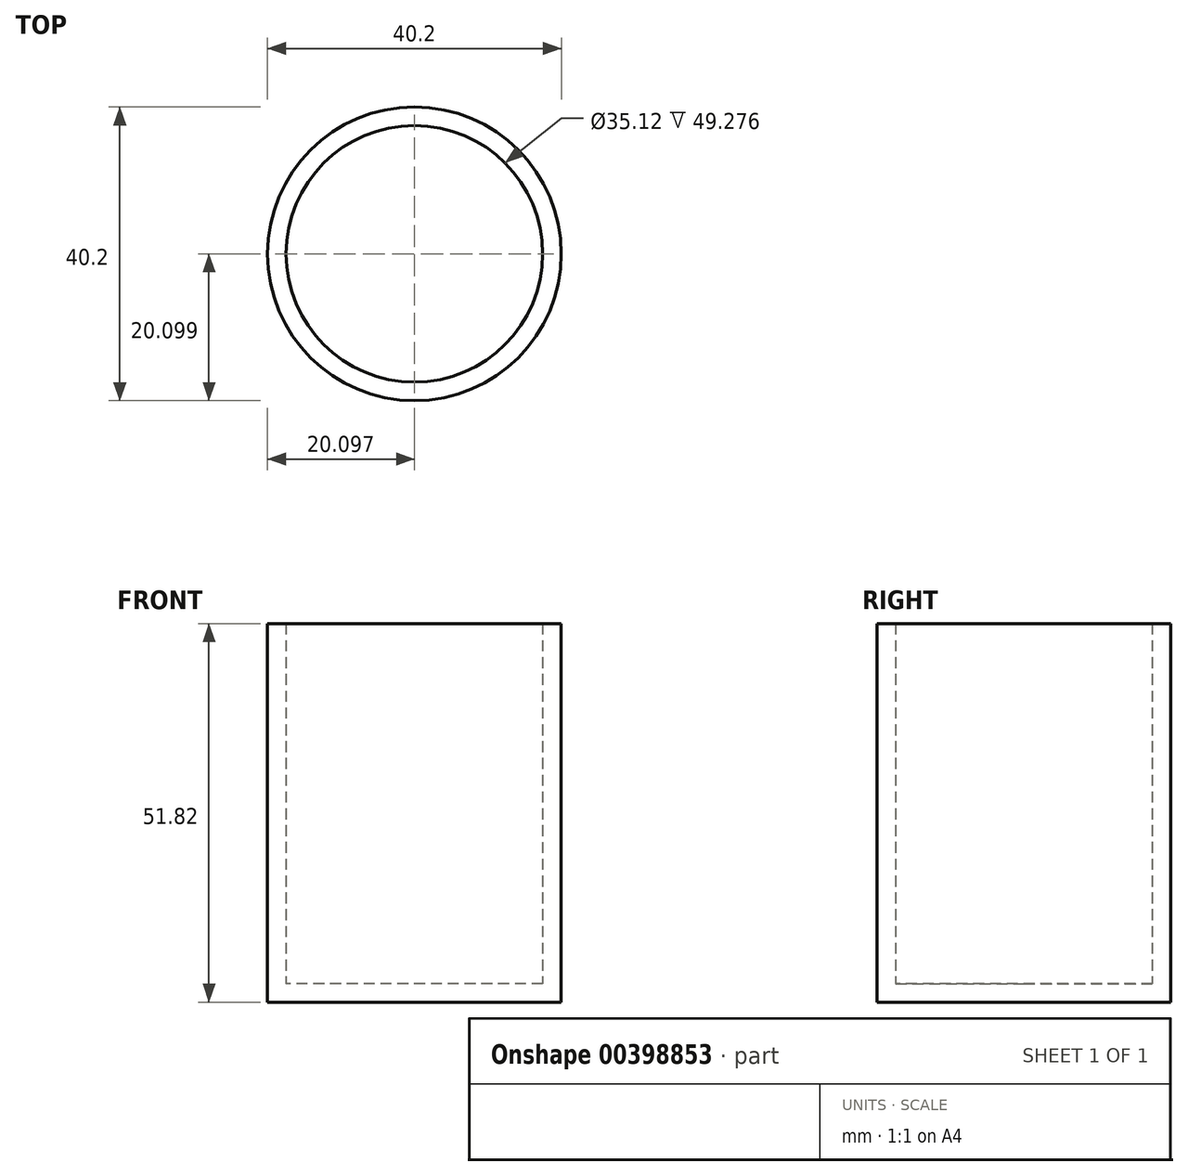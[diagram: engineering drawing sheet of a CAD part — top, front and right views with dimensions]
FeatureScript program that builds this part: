
annotation { "Feature Type Name" : "Feature", "Feature Type Description" : "" }
export const myFeature = defineFeature(function(context is Context, id is Id, definition is map)
    precondition{}
    {
        {
            var Q0;
            Q0=qCreatedBy(makeId("Top.planeOp"),FACE);
            var sketch = newSketch(context, id + "F0", { "sketchPlane" : qUnion([Q0])});
            skCircle(sketch, "E0", {"center": v(19.39, -5.3) * mm, "radius": 20.1 * mm});
            skPoint(sketch, "E0.first.point", {"position": v(0, 0) * mm});
            skPoint(sketch, "E0.second.point", {"position": v(24.03, -24.86) * mm});
            skPoint(sketch, "E0.third.point", {"position": v(0, -10.6) * mm});
            skSolve(sketch);
        }
        {
            var Q0;
            Q0=makeQuery(id+"F0.imprint","IMPRINT",FACE,{"disambiguationData":[TD([[makeQuery(id+"F0.imprint","IMPRINT",EDGE,{"derivedFrom":sQuery(id+"F0.wireOp",EDGE,"E0")}),1.0]])]});
            extrude(context, id + "F1", {"entities" : qUnion([Q0]), "depth" : 51.82 * mm});
        }
        {
            var Q0;
            Q0=makeQuery(id+"F1.opExtrude","CAP_FACE",FACE,{"disambiguationData":[OSD([sQuery(id+"F0.wireOp",EDGE,"E0")])],"isStart":false});
            shell(context, id + "F2", {"entities" : qUnion([Q0]), "thickness" : 2.54 * mm});
        }
    });
